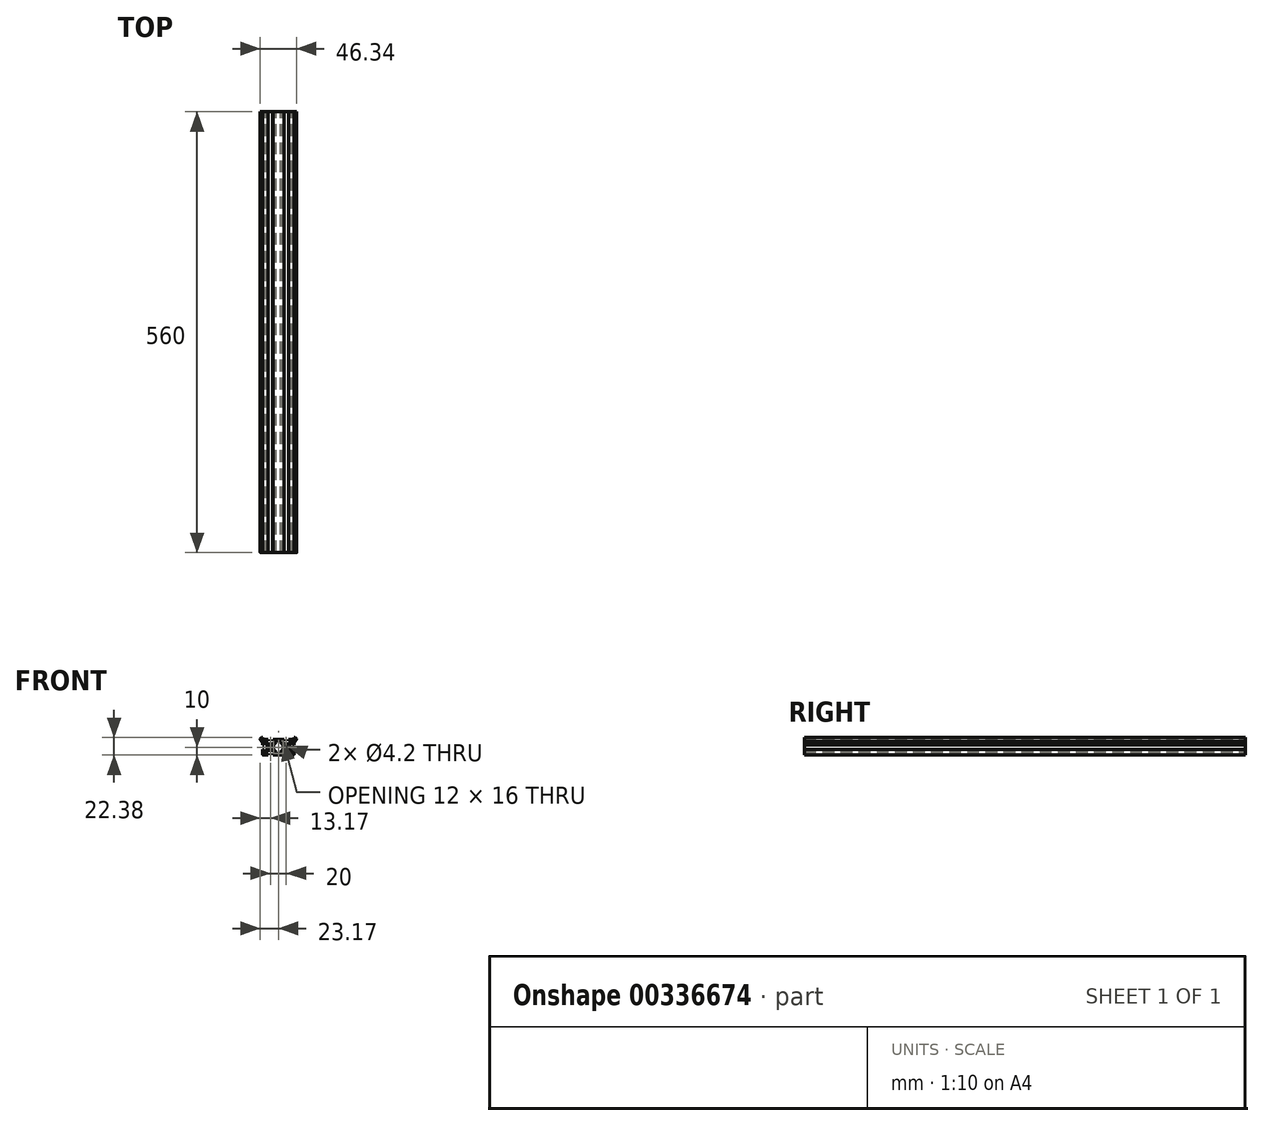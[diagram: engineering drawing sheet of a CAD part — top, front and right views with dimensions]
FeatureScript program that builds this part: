
annotation { "Feature Type Name" : "Feature", "Feature Type Description" : "" }
export const myFeature = defineFeature(function(context is Context, id is Id, definition is map)
    precondition{}
    {
        {
            var Q0;
            Q0=qCreatedBy(makeId("Front.planeOp"),FACE);
            var sketch = newSketch(context, id + "F0", { "sketchPlane" : qUnion([Q0])});
            skLineSegment(sketch, "E0.bottom", {"start": v(20, 10) * mm, "end": v(13, 10) * mm});
            skLineSegment(sketch, "E0.top", {"start": v(19, -10) * mm, "end": v(13, -10) * mm});
            skLineSegment(sketch, "E0.left", {"start": v(20, 7.12) * mm, "end": v(20, 3) * mm});
            skLineSegment(sketch, "E0.right", {"start": v(-20, 7.62) * mm, "end": v(-20, 3) * mm});
            skPoint(sketch, "E0.middle", {"position": v(0, 0) * mm});
            skLineSegment(sketch, "E1", {"start": v(-20, 0) * mm, "end": v(20, 0) * mm, "construction": true});
            skPoint(sketch, "E2", {"position": v(-10, 0) * mm});
            skPoint(sketch, "E3", {"position": v(10, 0) * mm});
            skCircle(sketch, "E4", {"center": v(10, 0) * mm, "radius": 2.1 * mm});
            skCircle(sketch, "E5", {"center": v(-10, 0) * mm, "radius": 2.1 * mm});
            skLineSegment(sketch, "E6.bottom", {"start": v(-7.06, 4) * mm, "end": v(-12.94, 4) * mm});
            skLineSegment(sketch, "E6.top", {"start": v(-7.06, -4) * mm, "end": v(-12.94, -4) * mm});
            skLineSegment(sketch, "E6.left", {"start": v(-6, 2.94) * mm, "end": v(-6, -2.94) * mm});
            skLineSegment(sketch, "E6.right", {"start": v(-14, 2.94) * mm, "end": v(-14, -2.94) * mm});
            skLineSegment(sketch, "E7.bottom", {"start": v(-19, -10) * mm, "end": v(-16, -10) * mm});
            skLineSegment(sketch, "E7.top", {"start": v(-18, -6) * mm, "end": v(-17.06, -6) * mm});
            skLineSegment(sketch, "E7.left", {"start": v(-20, -9) * mm, "end": v(-20, -6) * mm});
            skLineSegment(sketch, "E7.right", {"start": v(-16, -8) * mm, "end": v(-16, -7.06) * mm});
            skLineSegment(sketch, "E8.bottom", {"start": v(-20, 10) * mm, "end": v(-16, 10) * mm});
            skLineSegment(sketch, "E8.top", {"start": v(-18, 6) * mm, "end": v(-17.06, 6) * mm});
            skLineSegment(sketch, "E8.left", {"start": v(-20, 7.12) * mm, "end": v(-20, 6) * mm});
            skLineSegment(sketch, "E8.right", {"start": v(-16, 8) * mm, "end": v(-16, 7.06) * mm});
            skLineSegment(sketch, "E9", {"start": v(-16, -8) * mm, "end": v(-13, -8) * mm});
            skLineSegment(sketch, "E10.MirrorCS", {"start": v(-16, 8) * mm, "end": v(-13, 8) * mm});
            skLineSegment(sketch, "E11", {"start": v(-20, -3) * mm, "end": v(-18, -3) * mm});
            skLineSegment(sketch, "E12.MirrorCS", {"start": v(-20, 3) * mm, "end": v(-18, 3) * mm});
            skLineSegment(sketch, "E13.trimOffspring", {"start": v(-18, 6) * mm, "end": v(-18, 3) * mm});
            skLineSegment(sketch, "E14.trimOffspring", {"start": v(-18, -3) * mm, "end": v(-18, -6) * mm});
            skLineSegment(sketch, "E15", {"start": v(-13, -10) * mm, "end": v(-13, -8) * mm});
            skLineSegment(sketch, "E16.MirrorCS", {"start": v(-13, 10) * mm, "end": v(-13, 8) * mm});
            skPoint(sketch, "E17", {"position": v(-12.94, -4) * mm});
            skPoint(sketch, "E18.MirrorP", {"position": v(-7.06, -4) * mm});
            skPoint(sketch, "E19.MirrorP", {"position": v(-12.94, 4) * mm});
            skPoint(sketch, "E20.MirrorP", {"position": v(-7.06, 4) * mm});
            skLineSegment(sketch, "E21", {"start": v(-12.94, -4) * mm, "end": v(-16, -7.06) * mm});
            skPoint(sketch, "E22", {"position": v(-14, -2.94) * mm});
            skPoint(sketch, "E23", {"position": v(-14, 2.94) * mm});
            skLineSegment(sketch, "E24", {"start": v(-14, -2.94) * mm, "end": v(-17.06, -6) * mm});
            skLineSegment(sketch, "E25.MirrorCS", {"start": v(-14, 2.94) * mm, "end": v(-17.06, 6) * mm});
            skLineSegment(sketch, "E26.MirrorCS", {"start": v(-12.94, 4) * mm, "end": v(-16, 7.06) * mm});
            skLineSegment(sketch, "E27.MirrorCS", {"start": v(-7.06, 4) * mm, "end": v(-4, 7.06) * mm});
            skLineSegment(sketch, "E28.MirrorCS", {"start": v(-6, 2.94) * mm, "end": v(-2.94, 6) * mm});
            skLineSegment(sketch, "E29.MirrorCS", {"start": v(-7.06, -4) * mm, "end": v(-4, -7.06) * mm});
            skLineSegment(sketch, "E30.MirrorCS", {"start": v(-6, -2.94) * mm, "end": v(-2.94, -6) * mm});
            skLineSegment(sketch, "E31", {"start": v(-2.94, 6) * mm, "end": v(-2.94, 8) * mm});
            skLineSegment(sketch, "E32", {"start": v(-4, 7.06) * mm, "end": v(-4, 8) * mm});
            skLineSegment(sketch, "E33", {"start": v(-2.94, -6) * mm, "end": v(-2.94, -8) * mm});
            skLineSegment(sketch, "E34", {"start": v(-4, -7.06) * mm, "end": v(-4, -8) * mm});
            skArc(sketch, "E35.filletArc", {"start": v(-20, -9) * mm, "mid": v(-19.7, -9.7) * mm, "end": v(-19, -10) * mm});
            skLineSegment(sketch, "E36.MirrorCS", {"start": v(-7, -10) * mm, "end": v(-7, -8) * mm});
            skLineSegment(sketch, "E37.MirrorCS", {"start": v(-7, 10) * mm, "end": v(-7, 8) * mm});
            skLineSegment(sketch, "E38.trimOffspring", {"start": v(-13, 10) * mm, "end": v(-20, 10) * mm});
            skLineSegment(sketch, "E39.trimOffspring", {"start": v(-7, 8) * mm, "end": v(7, 8) * mm});
            skLineSegment(sketch, "E40.trimOffspring", {"start": v(-13, -10) * mm, "end": v(-19, -10) * mm});
            skLineSegment(sketch, "E41.trimOffspring", {"start": v(-7, -8) * mm, "end": v(-4, -8) * mm});
            skLineSegment(sketch, "E42.trimOffspring", {"start": v(-20, -3) * mm, "end": v(-20, -9) * mm});
            skLineSegment(sketch, "E43", {"start": v(-20, 10) * mm, "end": v(-20, 12.38) * mm});
            skPoint(sketch, "E44", {"position": v(-20, 7.62) * mm});
            skLineSegment(sketch, "E45", {"start": v(-20, 12.38) * mm, "end": v(-21, 12.38) * mm});
            skLineSegment(sketch, "E46", {"start": v(-20.5, 7.62) * mm, "end": v(-21, 7.62) * mm});
            skLineSegment(sketch, "E47", {"start": v(-21, 12.38) * mm, "end": v(-23.03, 10.35) * mm});
            skLineSegment(sketch, "E48", {"start": v(-21, 7.62) * mm, "end": v(-23.03, 9.65) * mm});
            skArc(sketch, "E49.filletArc", {"start": v(-20, 7.12) * mm, "mid": v(-20.15, 7.47) * mm, "end": v(-20.5, 7.62) * mm});
            skPoint(sketch, "E50.visualSharp", {"position": v(-23.38, 10) * mm});
            skArc(sketch, "E50.filletArc", {"start": v(-23.03, 10.35) * mm, "mid": v(-23.17, 10) * mm, "end": v(-23.03, 9.65) * mm});
            skLineSegment(sketch, "E51.trimOffspring", {"start": v(-2.94, -8) * mm, "end": v(4, -8) * mm});
            skLineSegment(sketch, "E52.MirrorCS", {"start": v(21, 7.62) * mm, "end": v(23.03, 9.65) * mm});
            skLineSegment(sketch, "E53.MirrorCS", {"start": v(21, 12.38) * mm, "end": v(23.03, 10.35) * mm});
            skArc(sketch, "E54.MirrorCS", {"start": v(23.03, 10.35) * mm, "mid": v(23.17, 10) * mm, "end": v(23.03, 9.65) * mm});
            skLineSegment(sketch, "E55.MirrorCS", {"start": v(20, 12.38) * mm, "end": v(21, 12.38) * mm});
            skLineSegment(sketch, "E56.MirrorCS", {"start": v(20, 10) * mm, "end": v(20, 12.38) * mm});
            skLineSegment(sketch, "E57.MirrorCS", {"start": v(20.5, 7.62) * mm, "end": v(21, 7.62) * mm});
            skArc(sketch, "E58.MirrorCS", {"start": v(20, 7.12) * mm, "mid": v(20.15, 7.47) * mm, "end": v(20.5, 7.62) * mm});
            skLineSegment(sketch, "E59.MirrorCS", {"start": v(18, -6) * mm, "end": v(17.06, -6) * mm});
            skLineSegment(sketch, "E60.MirrorCS", {"start": v(18, 6) * mm, "end": v(17.06, 6) * mm});
            skLineSegment(sketch, "E61.MirrorCS", {"start": v(16, -8) * mm, "end": v(16, -7.06) * mm});
            skLineSegment(sketch, "E62.MirrorCS", {"start": v(16, 8) * mm, "end": v(16, 7.06) * mm});
            skLineSegment(sketch, "E63.MirrorCS", {"start": v(4, -7.06) * mm, "end": v(4, -8) * mm});
            skLineSegment(sketch, "E64.MirrorCS", {"start": v(20, 7.12) * mm, "end": v(20, 6) * mm});
            skLineSegment(sketch, "E65.MirrorCS", {"start": v(20, -9) * mm, "end": v(20, -6) * mm});
            skArc(sketch, "E66.MirrorCS", {"start": v(20, -9) * mm, "mid": v(19.7, -9.7) * mm, "end": v(19, -10) * mm});
            skLineSegment(sketch, "E67.MirrorCS", {"start": v(18, 6) * mm, "end": v(18, 3) * mm});
            skPoint(sketch, "E68.MirrorP", {"position": v(14, -2.94) * mm});
            skLineSegment(sketch, "E69.MirrorCS", {"start": v(20, 10) * mm, "end": v(16, 10) * mm});
            skLineSegment(sketch, "E70.MirrorCS", {"start": v(12.94, 4) * mm, "end": v(16, 7.06) * mm});
            skLineSegment(sketch, "E71.MirrorCS", {"start": v(16, -8) * mm, "end": v(13, -8) * mm});
            skLineSegment(sketch, "E72.MirrorCS", {"start": v(14, -2.94) * mm, "end": v(17.06, -6) * mm});
            skPoint(sketch, "E73.MirrorP", {"position": v(12.94, -4) * mm});
            skLineSegment(sketch, "E74.MirrorCS", {"start": v(18, -3) * mm, "end": v(18, -6) * mm});
            skLineSegment(sketch, "E75.MirrorCS", {"start": v(6, -2.94) * mm, "end": v(2.94, -6) * mm});
            skPoint(sketch, "E76.MirrorP", {"position": v(12.94, 4) * mm});
            skLineSegment(sketch, "E77.MirrorCS", {"start": v(20, -3) * mm, "end": v(20, -9) * mm});
            skLineSegment(sketch, "E78.MirrorCS", {"start": v(19, -10) * mm, "end": v(16, -10) * mm});
            skLineSegment(sketch, "E79.MirrorCS", {"start": v(20, -3) * mm, "end": v(18, -3) * mm});
            skLineSegment(sketch, "E80.MirrorCS", {"start": v(12.94, -4) * mm, "end": v(16, -7.06) * mm});
            skLineSegment(sketch, "E81.MirrorCS", {"start": v(20, 3) * mm, "end": v(18, 3) * mm});
            skLineSegment(sketch, "E82.MirrorCS", {"start": v(13, -10) * mm, "end": v(19, -10) * mm});
            skLineSegment(sketch, "E83.MirrorCS", {"start": v(7, -8) * mm, "end": v(4, -8) * mm});
            skLineSegment(sketch, "E84.MirrorCS", {"start": v(7.06, -4) * mm, "end": v(12.94, -4) * mm});
            skLineSegment(sketch, "E85.MirrorCS", {"start": v(13, -10) * mm, "end": v(13, -8) * mm});
            skLineSegment(sketch, "E86.MirrorCS", {"start": v(14, 2.94) * mm, "end": v(17.06, 6) * mm});
            skLineSegment(sketch, "E87.MirrorCS", {"start": v(7, -10) * mm, "end": v(7, -8) * mm});
            skPoint(sketch, "E88.MirrorP", {"position": v(7.06, -4) * mm});
            skLineSegment(sketch, "E89.MirrorCS", {"start": v(13, 10) * mm, "end": v(20, 10) * mm});
            skLineSegment(sketch, "E90.MirrorCS", {"start": v(13, 10) * mm, "end": v(13, 8) * mm});
            skPoint(sketch, "E91.MirrorP", {"position": v(14, 2.94) * mm});
            skLineSegment(sketch, "E92.MirrorCS", {"start": v(2.94, -6) * mm, "end": v(2.94, -8) * mm});
            skLineSegment(sketch, "E93.MirrorCS", {"start": v(7.06, -4) * mm, "end": v(4, -7.06) * mm});
            skLineSegment(sketch, "E94.MirrorCS", {"start": v(14, 2.94) * mm, "end": v(14, -2.94) * mm});
            skLineSegment(sketch, "E95.MirrorCS", {"start": v(16, 8) * mm, "end": v(13, 8) * mm});
            skLineSegment(sketch, "E96.trimOffspring", {"start": v(13, 8) * mm, "end": v(16, 8) * mm});
            skLineSegment(sketch, "E97.trimOffspring", {"start": v(7, 10) * mm, "end": v(-7, 10) * mm});
            skLineSegment(sketch, "E98.trimOffspring", {"start": v(7, -10) * mm, "end": v(-7, -10) * mm});
            skLineSegment(sketch, "E99.trimOffspring", {"start": v(13, -8) * mm, "end": v(16, -8) * mm});
            skPoint(sketch, "E100.orphan", {"position": v(20, -8) * mm});
            skPoint(sketch, "E101.visualSharp", {"position": v(6, 4) * mm});
            skLineSegment(sketch, "E102", {"start": v(17.06, 6) * mm, "end": v(16, 7.06) * mm, "construction": true});
            skLineSegment(sketch, "E103", {"start": v(7.06, -4) * mm, "end": v(6, -2.94) * mm, "construction": true});
            skLineSegment(sketch, "E104", {"start": v(16.53, 6.53) * mm, "end": v(6.53, -3.47) * mm, "construction": true});
            skLineSegment(sketch, "E105.MirrorCS", {"start": v(6, -2.94) * mm, "end": v(6, 2.94) * mm});
            skLineSegment(sketch, "E106.MirrorCS", {"start": v(12.94, 4) * mm, "end": v(7.06, 4) * mm});
            skLineSegment(sketch, "E107.MirrorCS", {"start": v(7.06, 4) * mm, "end": v(4, 7.06) * mm});
            skLineSegment(sketch, "E108.MirrorCS", {"start": v(6, 2.94) * mm, "end": v(2.94, 6) * mm});
            skLineSegment(sketch, "E109.MirrorCS", {"start": v(4, 8) * mm, "end": v(4, 7.06) * mm});
            skLineSegment(sketch, "E110.MirrorCS", {"start": v(7, 10) * mm, "end": v(1, 10) * mm});
            skLineSegment(sketch, "E111.MirrorCS", {"start": v(7, 10) * mm, "end": v(7, 8) * mm});
            skLineSegment(sketch, "E112", {"start": v(2.94, 6) * mm, "end": v(2.94, 8) * mm});
            skSolve(sketch);
        }
        {
            var Q0;
            Q0 = qSketchRegion(id + "F0", true);
            extrude(context, id + "F1", {"entities" : qUnion([Q0]), "depth" : 560 * mm});
        }
    });
